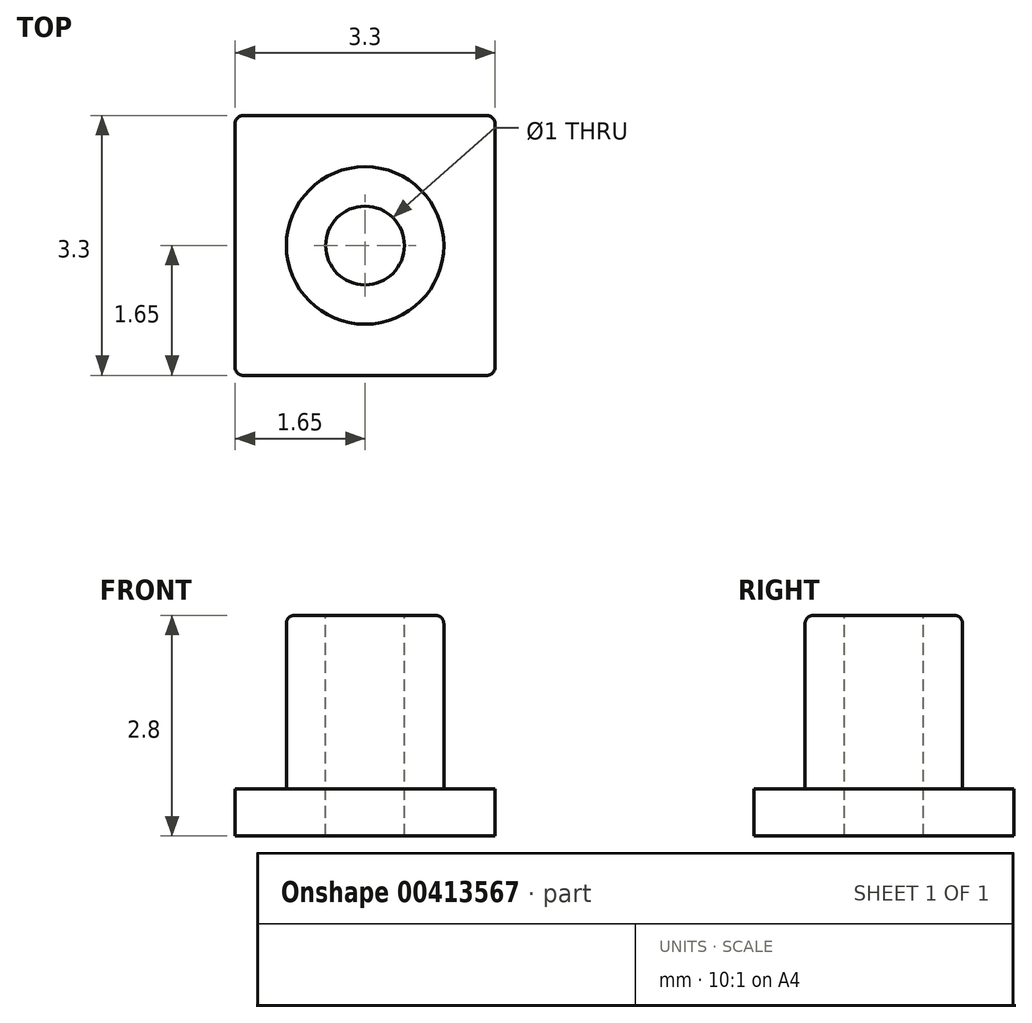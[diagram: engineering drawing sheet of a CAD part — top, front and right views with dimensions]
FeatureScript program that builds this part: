
annotation { "Feature Type Name" : "Feature", "Feature Type Description" : "" }
export const myFeature = defineFeature(function(context is Context, id is Id, definition is map)
    precondition{}
    {
        {
            var Q0;
            Q0=qCreatedBy(makeId("Top.planeOp"),FACE);
            var sketch = newSketch(context, id + "F0", { "sketchPlane" : qUnion([Q0])});
            skLineSegment(sketch, "E0.bottom", {"start": v(1.65, 1.65) * mm, "end": v(-1.65, 1.65) * mm});
            skLineSegment(sketch, "E0.top", {"start": v(1.65, -1.65) * mm, "end": v(-1.65, -1.65) * mm});
            skLineSegment(sketch, "E0.left", {"start": v(1.65, 1.65) * mm, "end": v(1.65, -1.65) * mm});
            skLineSegment(sketch, "E0.right", {"start": v(-1.65, 1.65) * mm, "end": v(-1.65, -1.65) * mm});
            skPoint(sketch, "E0.middle", {"position": v(0, 0) * mm});
            skSolve(sketch);
        }
        {
            var Q0;
            Q0=makeQuery(id+"F0.imprint","IMPRINT",FACE,{"disambiguationData":[TD([[makeQuery(id+"F0.imprint","IMPRINT",EDGE,{"derivedFrom":sQuery(id+"F0.wireOp",EDGE,"E0.bottom")}),1.0]])]});
            extrude(context, id + "F1", {"entities" : qUnion([Q0]), "depth" : 0.6 * mm});
        }
        {
            var Q0;
            Q0=makeQuery(id+"F1.opExtrude","CAP_FACE",FACE,{"disambiguationData":[OSD([sQuery(id+"F0.wireOp",EDGE,"E0.bottom"),sQuery(id+"F0.wireOp",EDGE,"E0.top"),sQuery(id+"F0.wireOp",EDGE,"E0.left"),sQuery(id+"F0.wireOp",EDGE,"E0.right")])],"isStart":false});
            var sketch = newSketch(context, id + "F2", { "sketchPlane" : qUnion([Q0])});
            skCircle(sketch, "E1", {"center": v(0, 0) * mm, "radius": 1 * mm});
            skSolve(sketch);
        }
        {
            var Q0;
            Q0=makeQuery(id+"F2.imprint","IMPRINT",FACE,{"disambiguationData":[TD([[makeQuery(id+"F2.imprint","IMPRINT",EDGE,{"derivedFrom":sQuery(id+"F2.wireOp",EDGE,"E1")}),1.0]])]});
            extrude(context, id + "F3", {"entities" : qUnion([Q0]), "operationType" : NewBodyOperationType.ADD, "depth" : 2.2 * mm});
        }
        {
            var Q0;
            Q0=makeQuery(id+"F3.opExtrude","CAP_FACE",FACE,{"disambiguationData":[OSD([sQuery(id+"F2.wireOp",EDGE,"E1")])],"isStart":false});
            var sketch = newSketch(context, id + "F4", { "sketchPlane" : qUnion([Q0])});
            skCircle(sketch, "E2", {"center": v(0, 0) * mm, "radius": 0.5 * mm});
            skSolve(sketch);
        }
        {
            var Q0;
            Q0=makeQuery(id+"F4.imprint","IMPRINT",FACE,{"disambiguationData":[TD([[makeQuery(id+"F4.imprint","IMPRINT",EDGE,{"derivedFrom":sQuery(id+"F4.wireOp",EDGE,"E2")}),1.0]])]});
            var Q1;
            Q1=makeQuery(id+"F1.opExtrude","CAP_FACE",FACE,{"disambiguationData":[OSD([sQuery(id+"F0.wireOp",EDGE,"E0.bottom"),sQuery(id+"F0.wireOp",EDGE,"E0.top"),sQuery(id+"F0.wireOp",EDGE,"E0.left"),sQuery(id+"F0.wireOp",EDGE,"E0.right")])],"isStart":true});
            extrude(context, id + "F5", {"entities" : qUnion([Q0]), "operationType" : NewBodyOperationType.REMOVE, "endBound" : BoundingType.UP_TO_SURFACE, "oppositeDirection" : true, "endBoundEntityFace" : qUnion([Q1]), "depth" : 25 * mm});
        }
        {
            var Q0;
            Q0=makeQuery(id+"F3.opExtrude","CAP_EDGE",EDGE,{"disambiguationData":[OSD([sQuery(id+"F2.wireOp",EDGE,"E1")])],"isStart":false});
            var Q1;
            Q1=makeQuery(id+"F5.boolean.opBoolean","COPY",EDGE,{"derivedFrom":makeQuery(id+"F5.opExtrude","CAP_EDGE",EDGE,{"disambiguationData":[OSD([sQuery(id+"F4.wireOp",EDGE,"E2")])],"isStart":true})});
            var Q2;
            Q2=makeQuery(id+"F3.opExtrude","CAP_EDGE",EDGE,{"disambiguationData":[OSD([sQuery(id+"F2.wireOp",EDGE,"E1")])],"isStart":true});
            var Q3;
            Q3=makeQuery(id+"F1.opExtrude","SWEPT_EDGE",EDGE,{"disambiguationData":[OSD([sQuery(id+"F0.wireOp",EDGE,"E0.top"),sQuery(id+"F0.wireOp",EDGE,"E0.right")])]});
            var Q4;
            Q4=makeQuery(id+"F1.opExtrude","SWEPT_EDGE",EDGE,{"disambiguationData":[OSD([sQuery(id+"F0.wireOp",EDGE,"E0.top"),sQuery(id+"F0.wireOp",EDGE,"E0.left")])]});
            var Q5;
            Q5=makeQuery(id+"F1.opExtrude","SWEPT_EDGE",EDGE,{"disambiguationData":[OSD([sQuery(id+"F0.wireOp",EDGE,"E0.bottom"),sQuery(id+"F0.wireOp",EDGE,"E0.right")])]});
            var Q6;
            Q6=makeQuery(id+"F1.opExtrude","SWEPT_EDGE",EDGE,{"disambiguationData":[OSD([sQuery(id+"F0.wireOp",EDGE,"E0.bottom"),sQuery(id+"F0.wireOp",EDGE,"E0.left")])]});
            var Q7;
            Q7=makeQuery(id+"F5.boolean.opBoolean","COPY",EDGE,{"derivedFrom":makeQuery(id+"F5.opExtrude","CAP_EDGE",EDGE,{"disambiguationData":[OSD([sQuery(id+"F4.wireOp",EDGE,"E2")])],"isStart":false})});
            fillet(context, id + "F6", {"entities" : qUnion([Q0, Q1, Q2, Q3, Q4, Q5, Q6, Q7]), "radius" : 0.1 * mm, "tangentPropagation" : true, "allowEdgeOverflow" : false});
        }
    });
